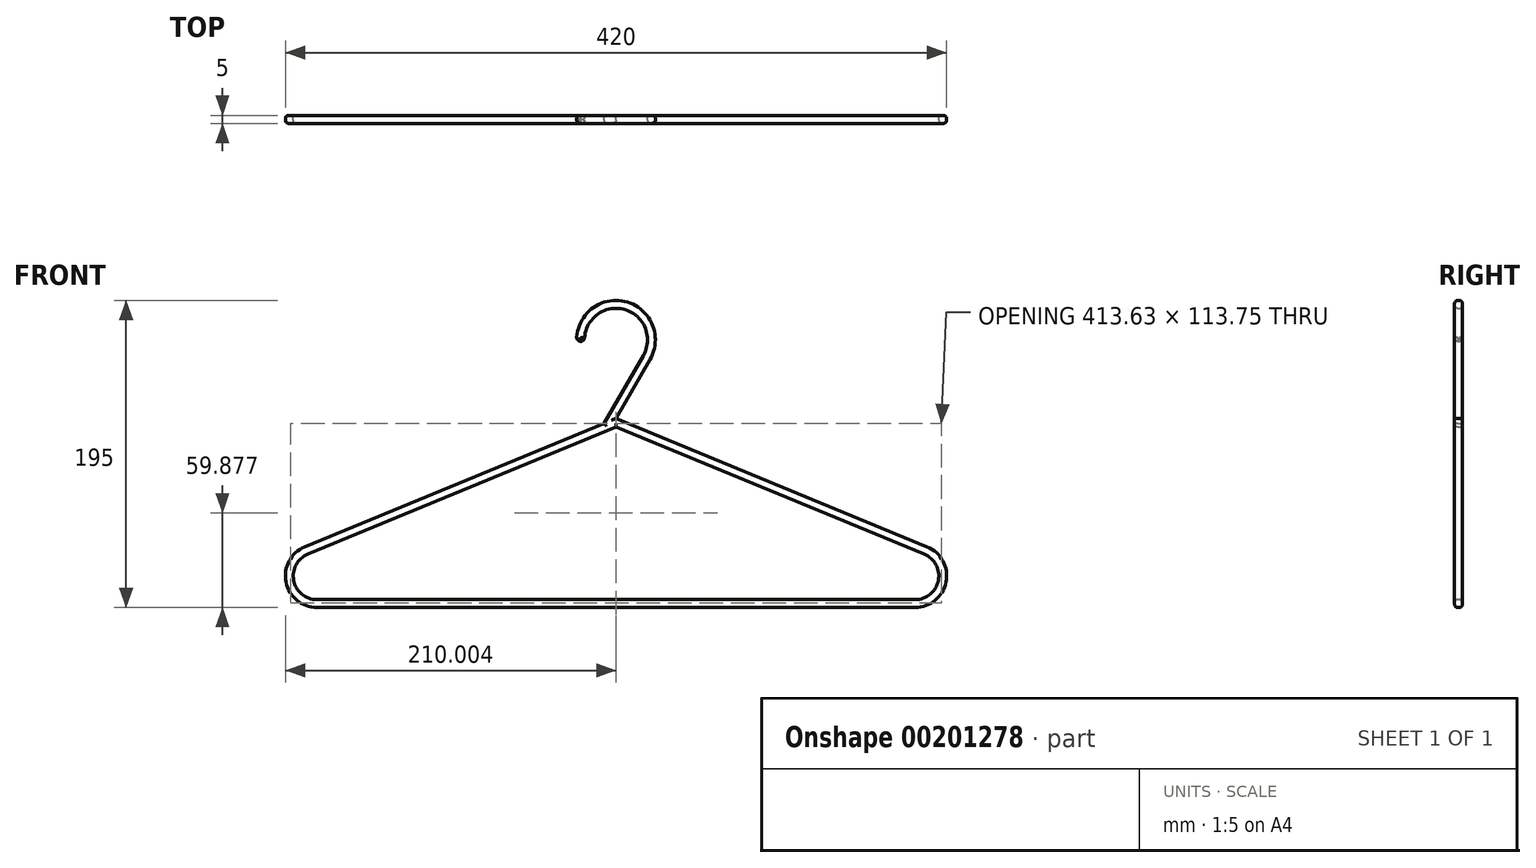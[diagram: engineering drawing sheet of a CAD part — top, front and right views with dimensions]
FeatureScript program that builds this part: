
annotation { "Feature Type Name" : "Feature", "Feature Type Description" : "" }
export const myFeature = defineFeature(function(context is Context, id is Id, definition is map)
    precondition{}
    {
        {
            var Q0;
            Q0=qCreatedBy(makeId("Front.planeOp"),FACE);
            var sketch = newSketch(context, id + "F3", { "sketchPlane" : qUnion([Q0])});
            skLineSegment(sketch, "E0", {"start": v(100.94, 0) * mm, "end": v(480.94, 0) * mm});
            skLineSegment(sketch, "E1", {"start": v(488.57, 38.49) * mm, "end": v(290.94, 120) * mm});
            skPoint(sketch, "E1.endSnap0", {"position": v(290.94, 0) * mm});
            skLineSegment(sketch, "E2", {"start": v(283.37, 116.87) * mm, "end": v(93.32, 38.49) * mm});
            skPoint(sketch, "E3.visualSharp", {"position": v(0, 0) * mm});
            skArc(sketch, "E3.filletArc", {"start": v(93.32, 38.49) * mm, "mid": v(81.33, 16.11) * mm, "end": v(100.94, 0) * mm});
            skPoint(sketch, "E4.visualSharp", {"position": v(581.89, 0) * mm});
            skArc(sketch, "E4.filletArc", {"start": v(480.94, 0) * mm, "mid": v(500.56, 16.11) * mm, "end": v(488.57, 38.49) * mm});
            skArc(sketch, "E5", {"start": v(312.6, 157.5) * mm, "mid": v(296.95, 194.27) * mm, "end": v(265.96, 169.03) * mm});
            skLineSegment(sketch, "E6", {"start": v(290.94, 120) * mm, "end": v(312.6, 157.5) * mm});
            skLineSegment(sketch, "E7.0", {"start": v(290.94, 114.6) * mm, "end": v(95.22, 33.87) * mm});
            skLineSegment(sketch, "E7.1", {"start": v(486.66, 33.87) * mm, "end": v(290.94, 114.6) * mm});
            skArc(sketch, "E7.2", {"start": v(95.22, 33.87) * mm, "mid": v(86.23, 17.08) * mm, "end": v(100.94, 5) * mm});
            skLineSegment(sketch, "E7.3", {"start": v(100.94, 5) * mm, "end": v(480.94, 5) * mm});
            skArc(sketch, "E7.4", {"start": v(480.94, 5) * mm, "mid": v(495.66, 17.08) * mm, "end": v(486.66, 33.87) * mm});
            skArc(sketch, "E8.0", {"start": v(308.26, 160) * mm, "mid": v(295.65, 189.44) * mm, "end": v(270.97, 169.03) * mm});
            skLineSegment(sketch, "E9.0", {"start": v(283.37, 116.87) * mm, "end": v(308.26, 160) * mm});
            skLineSegment(sketch, "E10", {"start": v(270.97, 169.03) * mm, "end": v(265.96, 169.03) * mm});
            skSolve(sketch);
        }
        {
            var Q0;
            Q0 = qSketchRegion(id + "F3", true);
            extrude(context, id + "F4", {"entities" : qUnion([Q0]), "depth" : 5 * mm});
        }
        {
            var Q0;
            Q0=makeQuery(id+"F4.opExtrude","CAP_EDGE",EDGE,{"disambiguationData":[OSD([sQuery(id+"F3.wireOp",EDGE,"E2")])],"isStart":false});
            var Q1;
            Q1=makeQuery(id+"F4.opExtrude","CAP_EDGE",EDGE,{"disambiguationData":[OSD([sQuery(id+"F3.wireOp",EDGE,"E6")])],"isStart":false});
            var Q2;
            Q2=makeQuery(id+"F4.opExtrude","CAP_EDGE",EDGE,{"disambiguationData":[OSD([sQuery(id+"F3.wireOp",EDGE,"E9.0")])],"isStart":false});
            var Q3;
            Q3=makeQuery(id+"F4.opExtrude","CAP_EDGE",EDGE,{"disambiguationData":[OSD([sQuery(id+"F3.wireOp",EDGE,"E8.0")])],"isStart":false});
            var Q4;
            Q4=makeQuery(id+"F4.opExtrude","CAP_EDGE",EDGE,{"disambiguationData":[OSD([sQuery(id+"F3.wireOp",EDGE,"E5")])],"isStart":false});
            var Q5;
            Q5=makeQuery(id+"F4.opExtrude","CAP_EDGE",EDGE,{"disambiguationData":[OSD([sQuery(id+"F3.wireOp",EDGE,"E5")])],"isStart":true});
            var Q6;
            Q6=makeQuery(id+"F4.opExtrude","CAP_EDGE",EDGE,{"disambiguationData":[OSD([sQuery(id+"F3.wireOp",EDGE,"E1")])],"isStart":false});
            var Q7;
            Q7=makeQuery(id+"F4.opExtrude","CAP_EDGE",EDGE,{"disambiguationData":[OSD([sQuery(id+"F3.wireOp",EDGE,"E7.0")])],"isStart":false});
            var Q8;
            Q8=makeQuery(id+"F4.opExtrude","CAP_EDGE",EDGE,{"disambiguationData":[OSD([sQuery(id+"F3.wireOp",EDGE,"E7.2")])],"isStart":false});
            var Q9;
            Q9=makeQuery(id+"F4.opExtrude","CAP_EDGE",EDGE,{"disambiguationData":[OSD([sQuery(id+"F3.wireOp",EDGE,"E3.filletArc")])],"isStart":false});
            var Q10;
            Q10=makeQuery(id+"F4.opExtrude","CAP_EDGE",EDGE,{"disambiguationData":[OSD([sQuery(id+"F3.wireOp",EDGE,"E7.3")])],"isStart":false});
            var Q11;
            Q11=makeQuery(id+"F4.opExtrude","CAP_EDGE",EDGE,{"disambiguationData":[OSD([sQuery(id+"F3.wireOp",EDGE,"E0")])],"isStart":false});
            var Q12;
            Q12=makeQuery(id+"F4.opExtrude","CAP_EDGE",EDGE,{"disambiguationData":[OSD([sQuery(id+"F3.wireOp",EDGE,"E4.filletArc")])],"isStart":false});
            var Q13;
            Q13=makeQuery(id+"F4.opExtrude","CAP_EDGE",EDGE,{"disambiguationData":[OSD([sQuery(id+"F3.wireOp",EDGE,"E7.4")])],"isStart":false});
            var Q14;
            Q14=makeQuery(id+"F4.opExtrude","CAP_EDGE",EDGE,{"disambiguationData":[OSD([sQuery(id+"F3.wireOp",EDGE,"E7.1")])],"isStart":false});
            fillet(context, id + "F0", {"entities" : qUnion([Q0, Q1, Q2, Q3, Q4, Q5, Q6, Q7, Q8, Q9, Q10, Q11, Q12, Q13, Q14]), "radius" : 2 * mm, "tangentPropagation" : true, "allowEdgeOverflow" : false});
        }
        {
            var Q0;
            Q0=makeQuery(id+"F0.opFillet","BLEND_EDGE",EDGE,{"blendedFrom":[makeQuery(id+"F4.opExtrude","CAP_EDGE",EDGE,{"disambiguationData":[OSD([sQuery(id+"F3.wireOp",EDGE,"E5")])],"isStart":false}),makeQuery(id+"F4.opExtrude","SWEPT_FACE",FACE,{"disambiguationData":[OSD([sQuery(id+"F3.wireOp",EDGE,"E10")])]})],"blendedInto":[makeQuery(id+"F4.opExtrude","SWEPT_FACE",FACE,{"disambiguationData":[OSD([sQuery(id+"F3.wireOp",EDGE,"E10")])]})]});
            var Q1;
            Q1=makeQuery(id+"F4.opExtrude","CAP_EDGE",EDGE,{"disambiguationData":[OSD([sQuery(id+"F3.wireOp",EDGE,"E10")])],"isStart":false});
            var Q2;
            Q2=makeQuery(id+"F0.opFillet","BLEND_EDGE",EDGE,{"blendedFrom":[makeQuery(id+"F4.opExtrude","CAP_EDGE",EDGE,{"disambiguationData":[OSD([sQuery(id+"F3.wireOp",EDGE,"E8.0")])],"isStart":false}),makeQuery(id+"F4.opExtrude","SWEPT_FACE",FACE,{"disambiguationData":[OSD([sQuery(id+"F3.wireOp",EDGE,"E10")])]})],"blendedInto":[makeQuery(id+"F4.opExtrude","SWEPT_FACE",FACE,{"disambiguationData":[OSD([sQuery(id+"F3.wireOp",EDGE,"E10")])]})]});
            var Q3;
            Q3=makeQuery(id+"F4.opExtrude","SWEPT_EDGE",EDGE,{"disambiguationData":[OSD([sQuery(id+"F3.wireOp",EDGE,"E8.0"),sQuery(id+"F3.wireOp",EDGE,"E10")])]});
            var Q4;
            Q4=makeQuery(id+"F4.opExtrude","CAP_EDGE",EDGE,{"disambiguationData":[OSD([sQuery(id+"F3.wireOp",EDGE,"E10")])],"isStart":true});
            var Q5;
            Q5=makeQuery(id+"F0.opFillet","BLEND_EDGE",EDGE,{"blendedFrom":[makeQuery(id+"F4.opExtrude","CAP_EDGE",EDGE,{"disambiguationData":[OSD([sQuery(id+"F3.wireOp",EDGE,"E5")])],"isStart":true}),makeQuery(id+"F4.opExtrude","SWEPT_FACE",FACE,{"disambiguationData":[OSD([sQuery(id+"F3.wireOp",EDGE,"E10")])]})],"blendedInto":[makeQuery(id+"F4.opExtrude","SWEPT_FACE",FACE,{"disambiguationData":[OSD([sQuery(id+"F3.wireOp",EDGE,"E10")])]})]});
            var Q6;
            Q6=makeQuery(id+"F4.opExtrude","SWEPT_EDGE",EDGE,{"disambiguationData":[OSD([sQuery(id+"F3.wireOp",EDGE,"E5"),sQuery(id+"F3.wireOp",EDGE,"E10")])]});
            fillet(context, id + "F1", {"entities" : qUnion([Q0, Q1, Q2, Q3, Q4, Q5, Q6]), "radius" : 2.5 * mm, "tangentPropagation" : true, "allowEdgeOverflow" : false});
        }
        {
            var Q0;
            Q0=makeQuery(id+"F4.opExtrude","CAP_EDGE",EDGE,{"disambiguationData":[OSD([sQuery(id+"F3.wireOp",EDGE,"E7.4")])],"isStart":true});
            var Q1;
            Q1=makeQuery(id+"F4.opExtrude","CAP_EDGE",EDGE,{"disambiguationData":[OSD([sQuery(id+"F3.wireOp",EDGE,"E4.filletArc")])],"isStart":true});
            var Q2;
            Q2=makeQuery(id+"F4.opExtrude","CAP_EDGE",EDGE,{"disambiguationData":[OSD([sQuery(id+"F3.wireOp",EDGE,"E1")])],"isStart":true});
            var Q3;
            Q3=makeQuery(id+"F4.opExtrude","CAP_EDGE",EDGE,{"disambiguationData":[OSD([sQuery(id+"F3.wireOp",EDGE,"E7.1")])],"isStart":true});
            var Q4;
            Q4=makeQuery(id+"F4.opExtrude","CAP_EDGE",EDGE,{"disambiguationData":[OSD([sQuery(id+"F3.wireOp",EDGE,"E7.3")])],"isStart":true});
            var Q5;
            Q5=makeQuery(id+"F4.opExtrude","CAP_EDGE",EDGE,{"disambiguationData":[OSD([sQuery(id+"F3.wireOp",EDGE,"E0")])],"isStart":true});
            var Q6;
            Q6=makeQuery(id+"F4.opExtrude","CAP_EDGE",EDGE,{"disambiguationData":[OSD([sQuery(id+"F3.wireOp",EDGE,"E7.2")])],"isStart":true});
            var Q7;
            Q7=makeQuery(id+"F4.opExtrude","CAP_EDGE",EDGE,{"disambiguationData":[OSD([sQuery(id+"F3.wireOp",EDGE,"E3.filletArc")])],"isStart":true});
            var Q8;
            Q8=makeQuery(id+"F4.opExtrude","CAP_EDGE",EDGE,{"disambiguationData":[OSD([sQuery(id+"F3.wireOp",EDGE,"E7.0")])],"isStart":true});
            var Q9;
            Q9=makeQuery(id+"F4.opExtrude","CAP_EDGE",EDGE,{"disambiguationData":[OSD([sQuery(id+"F3.wireOp",EDGE,"E2")])],"isStart":true});
            var Q10;
            Q10=makeQuery(id+"F4.opExtrude","CAP_EDGE",EDGE,{"disambiguationData":[OSD([sQuery(id+"F3.wireOp",EDGE,"E9.0")])],"isStart":true});
            var Q11;
            Q11=makeQuery(id+"F4.opExtrude","CAP_EDGE",EDGE,{"disambiguationData":[OSD([sQuery(id+"F3.wireOp",EDGE,"E8.0")])],"isStart":true});
            fillet(context, id + "F2", {"entities" : qUnion([Q0, Q1, Q2, Q3, Q4, Q5, Q6, Q7, Q8, Q9, Q10, Q11]), "radius" : 2 * mm, "tangentPropagation" : true, "allowEdgeOverflow" : false});
        }
    });
